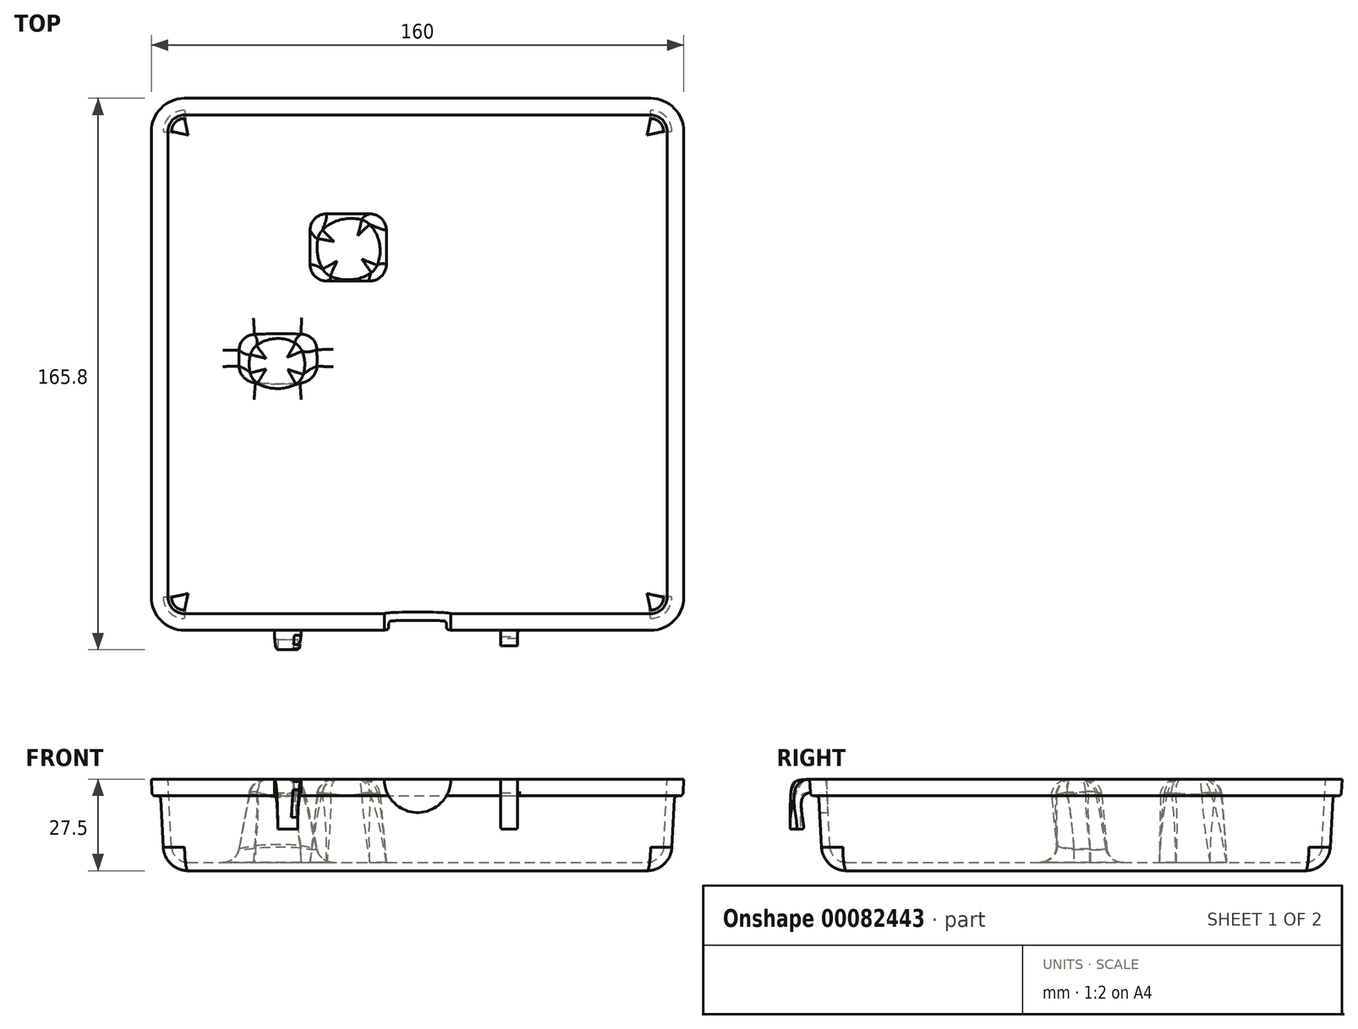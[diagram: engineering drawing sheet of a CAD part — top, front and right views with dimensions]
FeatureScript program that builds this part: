
annotation { "Feature Type Name" : "Feature", "Feature Type Description" : "" }
export const myFeature = defineFeature(function(context is Context, id is Id, definition is map)
    precondition{}
    {
        {
            var Q0;
            Q0=qCreatedBy(makeId("Top.planeOp"),FACE);
            var sketch = newSketch(context, id + "F0", { "sketchPlane" : qUnion([Q0])});
            skLineSegment(sketch, "E0.bottom", {"start": v(5, 0) * mm, "end": v(145, 0) * mm});
            skLineSegment(sketch, "E0.top", {"start": v(5, 150) * mm, "end": v(145, 150) * mm});
            skLineSegment(sketch, "E0.left", {"start": v(0, 5) * mm, "end": v(0, 145) * mm});
            skLineSegment(sketch, "E0.right", {"start": v(150, 5) * mm, "end": v(150, 145) * mm});
            skLineSegment(sketch, "E1.0", {"start": v(-5, 5) * mm, "end": v(-5, 145) * mm});
            skLineSegment(sketch, "E1.1", {"start": v(5, -5) * mm, "end": v(145, -5) * mm});
            skLineSegment(sketch, "E1.2", {"start": v(155, 5) * mm, "end": v(155, 145) * mm});
            skLineSegment(sketch, "E1.3", {"start": v(5, 155) * mm, "end": v(145, 155) * mm});
            skPoint(sketch, "E2.visualSharp", {"position": v(0, 150) * mm});
            skArc(sketch, "E2.filletArc", {"start": v(5, 150) * mm, "mid": v(1.46, 148.54) * mm, "end": v(0, 145) * mm});
            skPoint(sketch, "E3.visualSharp", {"position": v(150, 150) * mm});
            skArc(sketch, "E3.filletArc", {"start": v(150, 145) * mm, "mid": v(148.54, 148.54) * mm, "end": v(145, 150) * mm});
            skPoint(sketch, "E4.visualSharp", {"position": v(150, 0) * mm});
            skArc(sketch, "E4.filletArc", {"start": v(145, 0) * mm, "mid": v(148.54, 1.46) * mm, "end": v(150, 5) * mm});
            skPoint(sketch, "E5.visualSharp", {"position": v(0, 0) * mm});
            skArc(sketch, "E5.filletArc", {"start": v(0, 5) * mm, "mid": v(1.46, 1.46) * mm, "end": v(5, 0) * mm});
            skPoint(sketch, "E6.visualSharp", {"position": v(-5, 155) * mm});
            skArc(sketch, "E6.filletArc", {"start": v(5, 155) * mm, "mid": v(-2.07, 152.07) * mm, "end": v(-5, 145) * mm});
            skPoint(sketch, "E7.visualSharp", {"position": v(155, 155) * mm});
            skArc(sketch, "E7.filletArc", {"start": v(155, 145) * mm, "mid": v(152.07, 152.07) * mm, "end": v(145, 155) * mm});
            skPoint(sketch, "E8.visualSharp", {"position": v(155, -5) * mm});
            skArc(sketch, "E8.filletArc", {"start": v(145, -5) * mm, "mid": v(152.07, -2.07) * mm, "end": v(155, 5) * mm});
            skPoint(sketch, "E9.visualSharp", {"position": v(-5, -5) * mm});
            skArc(sketch, "E9.filletArc", {"start": v(-5, 5) * mm, "mid": v(-2.07, -2.07) * mm, "end": v(5, -5) * mm});
            skSolve(sketch);
        }
        {
            var Q0;
            Q0=makeQuery(id+"F0.imprint","IMPRINT",FACE,{"disambiguationData":[TD([[makeQuery(id+"F0.imprint","IMPRINT",EDGE,{"derivedFrom":sQuery(id+"F0.wireOp",EDGE,"E0.bottom")}),1.0]])]});
            extrude(context, id + "F1", {"entities" : qUnion([Q0]), "oppositeDirection" : true, "depth" : 25 * mm, "hasDraft" : true, "draftAngle" : 3 * degree, "draftPullDirection" : true});
        }
        {
            var Q0;
            Q0=makeQuery(id+"F1.opExtrude","SWEPT_EDGE",EDGE,{"disambiguationData":[OSD([sQuery(id+"F0.wireOp",EDGE,"E0.bottom"),sQuery(id+"F0.wireOp",EDGE,"E0.left")])]});
            var Q1;
            Q1=makeQuery(id+"F1.opExtrude","SWEPT_EDGE",EDGE,{"disambiguationData":[OSD([sQuery(id+"F0.wireOp",EDGE,"E0.bottom"),sQuery(id+"F0.wireOp",EDGE,"E0.right")])]});
            var Q2;
            Q2=makeQuery(id+"F1.opExtrude","SWEPT_EDGE",EDGE,{"disambiguationData":[OSD([sQuery(id+"F0.wireOp",EDGE,"E0.top"),sQuery(id+"F0.wireOp",EDGE,"E0.left")])]});
            var Q3;
            Q3=makeQuery(id+"F1.opExtrude","SWEPT_EDGE",EDGE,{"disambiguationData":[OSD([sQuery(id+"F0.wireOp",EDGE,"E0.top"),sQuery(id+"F0.wireOp",EDGE,"E0.right")])]});
            var Q4;
            Q4=makeQuery(id+"F1.opExtrude","CAP_FACE",FACE,{"disambiguationData":[OSD([sQuery(id+"F0.wireOp",EDGE,"E0.bottom"),sQuery(id+"F0.wireOp",EDGE,"E0.top"),sQuery(id+"F0.wireOp",EDGE,"E0.left"),sQuery(id+"F0.wireOp",EDGE,"E0.right")])],"isStart":false});
            fillet(context, id + "F2", {"entities" : qUnion([Q0, Q1, Q2, Q3, Q4]), "radius" : 5 * mm, "tangentPropagation" : true, "allowEdgeOverflow" : false});
        }
        {
            var Q0;
            Q0=makeQuery(id+"F1.opExtrude","CAP_FACE",FACE,{"disambiguationData":[OSD([sQuery(id+"F0.wireOp",EDGE,"E0.bottom"),sQuery(id+"F0.wireOp",EDGE,"E0.top"),sQuery(id+"F0.wireOp",EDGE,"E0.left"),sQuery(id+"F0.wireOp",EDGE,"E0.right")])],"isStart":true});
            shell(context, id + "F3", {"entities" : qUnion([Q0]), "thickness" : 2.5 * mm, "oppositeDirection" : true});
        }
        {
            var Q0;
            Q0=makeQuery(id+"F0.imprint","IMPRINT",FACE,{"disambiguationData":[TD([[makeQuery(id+"F0.imprint","IMPRINT",EDGE,{"derivedFrom":sQuery(id+"F0.wireOp",EDGE,"E0.bottom")}),-1.0]])]});
            extrude(context, id + "F4", {"entities" : qUnion([Q0]), "operationType" : NewBodyOperationType.ADD, "oppositeDirection" : true, "depth" : 5 * mm, "hasDraft" : true, "draftAngle" : 3 * degree, "draftPullDirection" : true});
        }
        {
            var Q0;
            {var subQ0=sQuery(id+"F0.wireOp",EDGE,"E0.bottom");Q0=makeQuery(id+"F4.boolean.opBoolean","INTERSECT",EDGE,{"derivedFrom":[makeQuery(id+"F1.opExtrude","SWEPT_FACE",FACE,{"disambiguationData":[OSD([subQ0])]}),makeQuery(id+"F4.opExtrude","CAP_FACE",FACE,{"disambiguationData":[OSD([subQ0,sQuery(id+"F0.wireOp",EDGE,"E0.top"),sQuery(id+"F0.wireOp",EDGE,"E0.left"),sQuery(id+"F0.wireOp",EDGE,"E0.right"),sQuery(id+"F0.wireOp",EDGE,"E1.0"),sQuery(id+"F0.wireOp",EDGE,"E1.1"),sQuery(id+"F0.wireOp",EDGE,"E1.2"),sQuery(id+"F0.wireOp",EDGE,"E1.3"),sQuery(id+"F0.wireOp",EDGE,"E2.filletArc"),sQuery(id+"F0.wireOp",EDGE,"E3.filletArc"),sQuery(id+"F0.wireOp",EDGE,"E4.filletArc"),sQuery(id+"F0.wireOp",EDGE,"E5.filletArc"),sQuery(id+"F0.wireOp",EDGE,"E6.filletArc"),sQuery(id+"F0.wireOp",EDGE,"E7.filletArc"),sQuery(id+"F0.wireOp",EDGE,"E8.filletArc"),sQuery(id+"F0.wireOp",EDGE,"E9.filletArc")])],"isStart":false})]});}
            var Q1;
            Q1=makeQuery(id+"F4.opExtrude","CAP_EDGE",EDGE,{"disambiguationData":[OSD([sQuery(id+"F0.wireOp",EDGE,"E1.1")])],"isStart":false});
            fillet(context, id + "F5", {"entities" : qUnion([Q0, Q1]), "radius" : 1 * mm, "tangentPropagation" : true, "allowEdgeOverflow" : false});
        }
        {
            var Q0;
            Q0=qCreatedBy(makeId("Front.planeOp"),FACE);
            var sketch = newSketch(context, id + "F6", { "sketchPlane" : qUnion([Q0])});
            skCircle(sketch, "E10", {"center": v(75, 0) * mm, "radius": 10 * mm});
            skSolve(sketch);
        }
        {
            var Q0;
            Q0 = qSketchRegion(id + "F6", true);
            extrude(context, id + "F7", {"entities" : qUnion([Q0]), "operationType" : NewBodyOperationType.REMOVE, "endBound" : BoundingType.SYMMETRIC, "depth" : 25 * mm});
        }
        {
            var Q0;
            Q0=qCreatedBy(makeId("Top.planeOp"),FACE);
            cPlane(context, id + "F8", {"entities" : qUnion([Q0]), "cplaneType" : CPlaneType.OFFSET, "offset" : 15 * mm, "oppositeDirection" : true, "width" : 150 * mm, "height" : 150 * mm});
        }
        {
            var Q0;
            {var subQ0=sQuery(id+"F0.wireOp",EDGE,"E1.1");var subQ1=sQuery(id+"F0.wireOp",EDGE,"E8.filletArc");Q0=makeQuery(id+"F7.boolean.opBoolean","SPLIT",FACE,{"disambiguationData":[TD([makeQuery(id+"F4.opExtrude","SWEPT_FACE",FACE,{"disambiguationData":[OSD([subQ1])]})])],"derivedFrom":makeQuery(id+"F4.opExtrude","SWEPT_FACE",FACE,{"disambiguationData":[OSD([subQ0])]})});}
            var sketch = newSketch(context, id + "F9", { "sketchPlane" : qUnion([Q0])});
            skLineSegment(sketch, "E11.bottom", {"start": v(100, 0.26) * mm, "end": v(105, 0.26) * mm});
            skLineSegment(sketch, "E11.top", {"start": v(100, -3.8) * mm, "end": v(105, -3.8) * mm});
            skLineSegment(sketch, "E11.left", {"start": v(100, 0.26) * mm, "end": v(100, -3.8) * mm});
            skLineSegment(sketch, "E11.right", {"start": v(105, 0.26) * mm, "end": v(105, -3.8) * mm});
            skSolve(sketch);
        }
        {
            var Q0;
            Q0=qCreatedBy(id+"F8.planeOp",FACE);
            var sketch = newSketch(context, id + "F10", { "sketchPlane" : qUnion([Q0])});
            skLineSegment(sketch, "E12.bottom", {"start": v(100, -6.79) * mm, "end": v(105, -6.79) * mm});
            skLineSegment(sketch, "E12.top", {"start": v(100, -8.79) * mm, "end": v(105, -8.79) * mm});
            skLineSegment(sketch, "E12.left", {"start": v(100, -6.79) * mm, "end": v(100, -8.79) * mm});
            skLineSegment(sketch, "E12.right", {"start": v(105, -6.79) * mm, "end": v(105, -8.79) * mm});
            skSolve(sketch);
        }
        {
            var Q1;
            Q1=makeQuery(id+"F9.imprint","IMPRINT",FACE,{"disambiguationData":[TD([[makeQuery(id+"F9.imprint","IMPRINT",EDGE,{"derivedFrom":sQuery(id+"F9.wireOp",EDGE,"E11.bottom")}),-1.0]])]});
            var Q2;
            Q2=makeQuery(id+"F10.imprint","IMPRINT",FACE,{"disambiguationData":[TD([[makeQuery(id+"F10.imprint","IMPRINT",EDGE,{"derivedFrom":sQuery(id+"F10.wireOp",EDGE,"E12.bottom")}),-1.0]])]});
            loft(context, id + "F11", {"operationType" : NewBodyOperationType.ADD, "startCondition" : LoftEndDerivativeType.NORMAL_TO_PROFILE, "startMagnitude" : 4, "endCondition" : LoftEndDerivativeType.NORMAL_TO_PROFILE, "endMagnitude" : 1, "sheetProfilesArray" : [{ "sheetProfileEntities" : qUnion([Q1]) }, { "sheetProfileEntities" : qUnion([Q2]) }]});
        }
        {
            var Q0;
            Q0=makeQuery(id+"F11.opLoft","MID_CAP_EDGE",EDGE,{"disambiguationData":[OSD([sQuery(id+"F0.wireOp",EDGE,"E1.1"),sQuery(id+"F9.wireOp",EDGE,"E11.bottom"),sQuery(id+"F9.wireOp",EDGE,"E11.top"),sQuery(id+"F9.wireOp",EDGE,"E11.right")])],"capPos":0.0});
            fillet(context, id + "F12", {"entities" : qUnion([Q0]), "radius" : 1 * mm, "tangentPropagation" : true, "allowEdgeOverflow" : false});
        }
        {
            var Q0;
            Q0=makeQuery(id+"F11.opLoft","CAP_FACE",FACE,{"disambiguationData":[OSD([makeQuery(id+"F10.imprint","IMPRINT",FACE,{"disambiguationData":[TD([[makeQuery(id+"F10.imprint","IMPRINT",EDGE,{"derivedFrom":sQuery(id+"F10.wireOp",EDGE,"E12.bottom")}),-1.0]])]})])],"isStart":true});
            fillet(context, id + "F13", {"entities" : qUnion([Q0]), "radius" : .5 * mm, "tangentPropagation" : true, "allowEdgeOverflow" : false});
        }
        {
            var Q0;
            Q0=makeQuery(id+"F3.opShell","OFFSET_FACE",FACE,{"disambiguationData":[OSD([sQuery(id+"F0.wireOp",EDGE,"E0.bottom"),sQuery(id+"F0.wireOp",EDGE,"E0.top"),sQuery(id+"F0.wireOp",EDGE,"E0.left"),sQuery(id+"F0.wireOp",EDGE,"E0.right"),sQuery(id+"F0.wireOp",EDGE,"E2.filletArc"),sQuery(id+"F0.wireOp",EDGE,"E3.filletArc"),sQuery(id+"F0.wireOp",EDGE,"E4.filletArc"),sQuery(id+"F0.wireOp",EDGE,"E5.filletArc")])]});
            var sketch = newSketch(context, id + "F14", { "sketchPlane" : qUnion([Q0])});
            skLineSegment(sketch, "E13.bottom", {"start": v(42.7, 100.07) * mm, "end": v(65.63, 100.07) * mm});
            skLineSegment(sketch, "E13.top", {"start": v(42.7, 120.25) * mm, "end": v(65.63, 120.25) * mm});
            skLineSegment(sketch, "E13.left", {"start": v(42.7, 100.07) * mm, "end": v(42.7, 120.25) * mm});
            skLineSegment(sketch, "E13.right", {"start": v(65.63, 100.07) * mm, "end": v(65.63, 120.25) * mm});
            skSolve(sketch);
        }
        {
            var Q0;
            Q0=qCreatedBy(makeId("Top.planeOp"),FACE);
            var sketch = newSketch(context, id + "F15", { "sketchPlane" : qUnion([Q0])});
            skArc(sketch, "E14", {"start": v(48.26, 102.79) * mm, "mid": v(55.2, 100.54) * mm, "end": v(61.55, 104.16) * mm});
            skArc(sketch, "E15", {"start": v(58.35, 117.61) * mm, "mid": v(51.16, 118.02) * mm, "end": v(45.95, 113.06) * mm});
            skArc(sketch, "E16", {"start": v(45.95, 113.06) * mm, "mid": v(45.46, 107.55) * mm, "end": v(48.26, 102.79) * mm});
            skArc(sketch, "E17", {"start": v(61.55, 104.16) * mm, "mid": v(63.08, 111.63) * mm, "end": v(58.35, 117.61) * mm});
            skSolve(sketch);
        }
        {
            var Q1;
            Q1=makeQuery(id+"F14.imprint","IMPRINT",FACE,{"disambiguationData":[TD([[makeQuery(id+"F14.imprint","IMPRINT",EDGE,{"derivedFrom":sQuery(id+"F14.wireOp",EDGE,"E13.bottom")}),1.0]])]});
            var Q2;
            Q2=makeQuery(id+"F15.imprint","IMPRINT",FACE,{"disambiguationData":[TD([[makeQuery(id+"F15.imprint","IMPRINT",EDGE,{"derivedFrom":sQuery(id+"F15.wireOp",EDGE,"E14")}),1.0]])]});
            var Q3;
            Q3=sQuery(id+"F14.wireOp",VERTEX,"E13.right.start");
            var Q4;
            Q4=sQuery(id+"F15.wireOp",VERTEX,"E16.end");
            loft(context, id + "F16", {"operationType" : NewBodyOperationType.ADD, "sheetProfilesArray" : [{ "sheetProfileEntities" : qUnion([Q1]) }, { "sheetProfileEntities" : qUnion([Q2]) }], "connections" : [{ "connectionEntities" : qUnion([Q3, Q4]), "connectionEdgeQueries" : qUnion([]), "connectionEdgeParameters" : [] }]});
        }
        {
            var Q0;
            Q0=makeQuery(id+"F16.opLoft","SWEPT_EDGE",EDGE,{"disambiguationData":[OSD([sQuery(id+"F14.wireOp",EDGE,"E13.bottom"),sQuery(id+"F14.wireOp",EDGE,"E13.left"),sQuery(id+"F15.wireOp",EDGE,"E14"),sQuery(id+"F15.wireOp",EDGE,"E16")])]});
            var Q1;
            Q1=makeQuery(id+"F16.opLoft","SWEPT_EDGE",EDGE,{"disambiguationData":[OSD([sQuery(id+"F14.wireOp",EDGE,"E13.bottom"),sQuery(id+"F14.wireOp",EDGE,"E13.right"),sQuery(id+"F15.wireOp",EDGE,"E14"),sQuery(id+"F15.wireOp",EDGE,"E17")])]});
            var Q2;
            Q2=makeQuery(id+"F16.opLoft","SWEPT_EDGE",EDGE,{"disambiguationData":[OSD([sQuery(id+"F14.wireOp",EDGE,"E13.top"),sQuery(id+"F14.wireOp",EDGE,"E13.right"),sQuery(id+"F15.wireOp",EDGE,"E15"),sQuery(id+"F15.wireOp",EDGE,"E17")])]});
            var Q3;
            Q3=makeQuery(id+"F16.opLoft","SWEPT_EDGE",EDGE,{"disambiguationData":[OSD([sQuery(id+"F14.wireOp",EDGE,"E13.top"),sQuery(id+"F14.wireOp",EDGE,"E13.left"),sQuery(id+"F15.wireOp",EDGE,"E15"),sQuery(id+"F15.wireOp",EDGE,"E16")])]});
            fillet(context, id + "F17", {"entities" : qUnion([Q0, Q1, Q2, Q3]), "radius" : 5 * mm, "tangentPropagation" : true, "allowEdgeOverflow" : false});
        }
        {
            var Q0;
            Q0=makeQuery(id+"F16.opLoft","MID_CAP_EDGE",EDGE,{"disambiguationData":[OSD([sQuery(id+"F14.wireOp",EDGE,"E13.bottom"),sQuery(id+"F14.wireOp",EDGE,"E13.top"),sQuery(id+"F14.wireOp",EDGE,"E13.left")])],"capPos":0.0});
            var Q1;
            Q1=makeQuery(id+"F16.opLoft","MID_CAP_EDGE",EDGE,{"disambiguationData":[OSD([sQuery(id+"F15.wireOp",EDGE,"E14"),sQuery(id+"F15.wireOp",EDGE,"E15"),sQuery(id+"F15.wireOp",EDGE,"E16")])],"capPos":1.0});
            fillet(context, id + "F18", {"entities" : qUnion([Q0, Q1]), "radius" : 5 * mm, "tangentPropagation" : true, "allowEdgeOverflow" : false});
        }
        {
            var Q0;
            Q0=makeQuery(id+"F14.imprint","IMPRINT",FACE,{"disambiguationData":[TD([[makeQuery(id+"F14.imprint","IMPRINT",EDGE,{"derivedFrom":sQuery(id+"F14.wireOp",EDGE,"E13.bottom")}),-1.0]])]});
            var sketch = newSketch(context, id + "F19", { "sketchPlane" : qUnion([Q0])});
            skLineSegment(sketch, "E18.bottom", {"start": v(20.62, 69.63) * mm, "end": v(45.62, 69.63) * mm});
            skLineSegment(sketch, "E18.top", {"start": v(20.62, 84.63) * mm, "end": v(45.62, 84.63) * mm});
            skLineSegment(sketch, "E18.left", {"start": v(20.62, 69.63) * mm, "end": v(20.62, 84.63) * mm});
            skLineSegment(sketch, "E18.right", {"start": v(45.62, 69.63) * mm, "end": v(45.62, 84.63) * mm});
            skSolve(sketch);
        }
        {
            var Q0;
            Q0=qCreatedBy(makeId("Top.planeOp"),FACE);
            var sketch = newSketch(context, id + "F20", { "sketchPlane" : qUnion([Q0])});
            skArc(sketch, "E19", {"start": v(38.94, 70.46) * mm, "mid": v(40.28, 75.1) * mm, "end": v(38.54, 79.62) * mm});
            skArc(sketch, "E20", {"start": v(38.54, 79.62) * mm, "mid": v(32.07, 82.32) * mm, "end": v(26.16, 78.56) * mm});
            skArc(sketch, "E21", {"start": v(26.16, 78.56) * mm, "mid": v(25.14, 74.72) * mm, "end": v(26.21, 70.9) * mm});
            skArc(sketch, "E22", {"start": v(26.21, 70.9) * mm, "mid": v(32.46, 67.2) * mm, "end": v(38.94, 70.46) * mm});
            skLineSegment(sketch, "E23", {"start": v(26.16, 78.56) * mm, "end": v(32.72, 74.78) * mm, "construction": true});
            skLineSegment(sketch, "E24", {"start": v(38.54, 79.62) * mm, "end": v(32.72, 74.78) * mm, "construction": true});
            skLineSegment(sketch, "E25", {"start": v(38.94, 70.46) * mm, "end": v(32.72, 74.78) * mm, "construction": true});
            skLineSegment(sketch, "E26", {"start": v(32.72, 74.78) * mm, "end": v(26.21, 70.9) * mm, "construction": true});
            skLineSegment(sketch, "E27", {"start": v(32.72, 74.78) * mm, "end": v(18.64, 74.78) * mm, "construction": true});
            skSolve(sketch);
        }
        {
            var Q1;
            Q1=makeQuery(id+"F19.imprint","IMPRINT",FACE,{"disambiguationData":[TD([[makeQuery(id+"F19.imprint","IMPRINT",EDGE,{"derivedFrom":sQuery(id+"F19.wireOp",EDGE,"E18.bottom")}),1.0]])]});
            var Q2;
            Q2=makeQuery(id+"F20.imprint","IMPRINT",FACE,{"disambiguationData":[TD([[makeQuery(id+"F20.imprint","IMPRINT",EDGE,{"derivedFrom":sQuery(id+"F20.wireOp",EDGE,"E19")}),1.0]])]});
            loft(context, id + "F21", {"operationType" : NewBodyOperationType.ADD, "sheetProfilesArray" : [{ "sheetProfileEntities" : qUnion([Q1]) }, { "sheetProfileEntities" : qUnion([Q2]) }]});
        }
        {
            var Q0;
            Q0=makeQuery(id+"F21.opLoft","SWEPT_EDGE",EDGE,{"disambiguationData":[OSD([sQuery(id+"F19.wireOp",EDGE,"E18.bottom"),sQuery(id+"F19.wireOp",EDGE,"E18.left"),sQuery(id+"F20.wireOp",EDGE,"E21"),sQuery(id+"F20.wireOp",EDGE,"E22")])]});
            var Q1;
            Q1=makeQuery(id+"F21.opLoft","SWEPT_EDGE",EDGE,{"disambiguationData":[OSD([sQuery(id+"F19.wireOp",EDGE,"E18.bottom"),sQuery(id+"F19.wireOp",EDGE,"E18.right"),sQuery(id+"F20.wireOp",EDGE,"E19"),sQuery(id+"F20.wireOp",EDGE,"E22")])]});
            var Q2;
            Q2=makeQuery(id+"F21.opLoft","SWEPT_EDGE",EDGE,{"disambiguationData":[OSD([sQuery(id+"F19.wireOp",EDGE,"E18.top"),sQuery(id+"F19.wireOp",EDGE,"E18.right"),sQuery(id+"F20.wireOp",EDGE,"E19"),sQuery(id+"F20.wireOp",EDGE,"E20")])]});
            var Q3;
            Q3=makeQuery(id+"F21.opLoft","SWEPT_EDGE",EDGE,{"disambiguationData":[OSD([sQuery(id+"F19.wireOp",EDGE,"E18.top"),sQuery(id+"F19.wireOp",EDGE,"E18.left"),sQuery(id+"F20.wireOp",EDGE,"E20"),sQuery(id+"F20.wireOp",EDGE,"E21")])]});
            fillet(context, id + "F22", {"entities" : qUnion([Q0, Q1, Q2, Q3]), "radius" : 5 * mm, "tangentPropagation" : true, "allowEdgeOverflow" : false});
        }
        {
            var Q0;
            Q0=makeQuery(id+"F22.opFillet","BLEND_EDGE",EDGE,{"blendedFrom":[makeQuery(id+"F21.opLoft","SWEPT_EDGE",EDGE,{"disambiguationData":[OSD([sQuery(id+"F19.wireOp",EDGE,"E18.bottom"),sQuery(id+"F19.wireOp",EDGE,"E18.right"),sQuery(id+"F20.wireOp",EDGE,"E19"),sQuery(id+"F20.wireOp",EDGE,"E22")])]}),makeQuery(id+"F3.opShell","OFFSET_FACE",FACE,{"disambiguationData":[OSD([sQuery(id+"F0.wireOp",EDGE,"E0.bottom"),sQuery(id+"F0.wireOp",EDGE,"E0.top"),sQuery(id+"F0.wireOp",EDGE,"E0.left"),sQuery(id+"F0.wireOp",EDGE,"E0.right"),sQuery(id+"F0.wireOp",EDGE,"E2.filletArc"),sQuery(id+"F0.wireOp",EDGE,"E3.filletArc"),sQuery(id+"F0.wireOp",EDGE,"E4.filletArc"),sQuery(id+"F0.wireOp",EDGE,"E5.filletArc")])]})],"blendedInto":[makeQuery(id+"F3.opShell","OFFSET_FACE",FACE,{"disambiguationData":[OSD([sQuery(id+"F0.wireOp",EDGE,"E0.bottom"),sQuery(id+"F0.wireOp",EDGE,"E0.top"),sQuery(id+"F0.wireOp",EDGE,"E0.left"),sQuery(id+"F0.wireOp",EDGE,"E0.right"),sQuery(id+"F0.wireOp",EDGE,"E2.filletArc"),sQuery(id+"F0.wireOp",EDGE,"E3.filletArc"),sQuery(id+"F0.wireOp",EDGE,"E4.filletArc"),sQuery(id+"F0.wireOp",EDGE,"E5.filletArc")])]})]});
            var Q1;
            Q1=makeQuery(id+"F21.opLoft","MID_CAP_EDGE",EDGE,{"disambiguationData":[OSD([sQuery(id+"F20.wireOp",EDGE,"E19"),sQuery(id+"F20.wireOp",EDGE,"E21"),sQuery(id+"F20.wireOp",EDGE,"E22")])],"capPos":1.0});
            fillet(context, id + "F23", {"entities" : qUnion([Q0, Q1]), "radius" : 5 * mm, "tangentPropagation" : true, "allowEdgeOverflow" : false});
        }
        {
            var Q0;
            {var subQ0=sQuery(id+"F0.wireOp",EDGE,"E1.1");var subQ1=sQuery(id+"F0.wireOp",EDGE,"E9.filletArc");Q0=makeQuery(id+"F7.boolean.opBoolean","SPLIT",FACE,{"disambiguationData":[TD([makeQuery(id+"F4.opExtrude","SWEPT_FACE",FACE,{"disambiguationData":[OSD([subQ1])]})])],"derivedFrom":makeQuery(id+"F4.opExtrude","SWEPT_FACE",FACE,{"disambiguationData":[OSD([subQ0])]})});}
            var sketch = newSketch(context, id + "F24", { "sketchPlane" : qUnion([Q0])});
            skLineSegment(sketch, "E28.bottom", {"start": v(32, -3.8) * mm, "end": v(40, -3.8) * mm});
            skLineSegment(sketch, "E28.top", {"start": v(32, 0.26) * mm, "end": v(40, 0.26) * mm});
            skLineSegment(sketch, "E28.left", {"start": v(32, -3.8) * mm, "end": v(32, 0.26) * mm});
            skLineSegment(sketch, "E28.right", {"start": v(40, -3.8) * mm, "end": v(40, 0.26) * mm});
            skLineSegment(sketch, "E29.bottom", {"start": v(38, 0.76) * mm, "end": v(42, 0.76) * mm});
            skLineSegment(sketch, "E29.top", {"start": v(38, 2.76) * mm, "end": v(42, 2.76) * mm});
            skLineSegment(sketch, "E29.left", {"start": v(38, 0.76) * mm, "end": v(38, 2.76) * mm});
            skLineSegment(sketch, "E29.right", {"start": v(42, 0.76) * mm, "end": v(42, 2.76) * mm});
            skSolve(sketch);
        }
        {
            var Q0;
            Q0=qCreatedBy(id+"F8.planeOp",FACE);
            var sketch = newSketch(context, id + "F25", { "sketchPlane" : qUnion([Q0])});
            skLineSegment(sketch, "E30.bottom", {"start": v(33, -7.79) * mm, "end": v(39, -7.79) * mm});
            skLineSegment(sketch, "E30.top", {"start": v(33, -10.79) * mm, "end": v(39, -10.79) * mm});
            skLineSegment(sketch, "E30.left", {"start": v(33, -7.79) * mm, "end": v(33, -10.79) * mm});
            skLineSegment(sketch, "E30.right", {"start": v(39, -7.79) * mm, "end": v(39, -10.79) * mm});
            skLineSegment(sketch, "E31.bottom", {"start": v(37, -11.04) * mm, "end": v(42.04, -11.04) * mm});
            skLineSegment(sketch, "E31.top", {"start": v(37, -13.04) * mm, "end": v(42.04, -13.04) * mm});
            skLineSegment(sketch, "E31.left", {"start": v(37, -11.04) * mm, "end": v(37, -13.04) * mm});
            skLineSegment(sketch, "E31.right", {"start": v(42.04, -11.04) * mm, "end": v(42.04, -13.04) * mm});
            skSolve(sketch);
        }
        {
            var Q1;
            {var subQ0=sQuery(id+"F24.wireOp",EDGE,"E28.left");Q1=makeQuery(id+"F24.imprint","IMPRINT",FACE,{"disambiguationData":[TD([[makeQuery(id+"F24.imprint","IMPRINT",EDGE,{"derivedFrom":subQ0}),-1.0]])]});}
            var Q2;
            Q2=makeQuery(id+"F25.imprint","IMPRINT",FACE,{"disambiguationData":[TD([[makeQuery(id+"F25.imprint","IMPRINT",EDGE,{"derivedFrom":sQuery(id+"F25.wireOp",EDGE,"E30.bottom")}),-1.0]])]});
            loft(context, id + "F26", {"operationType" : NewBodyOperationType.ADD, "startCondition" : LoftEndDerivativeType.NORMAL_TO_PROFILE, "startMagnitude" : 2.5, "endCondition" : LoftEndDerivativeType.NORMAL_TO_PROFILE, "endMagnitude" : 3, "sheetProfilesArray" : [{ "sheetProfileEntities" : qUnion([Q1]) }, { "sheetProfileEntities" : qUnion([Q2]) }]});
        }
        {
            var Q1;
            Q1=makeQuery(id+"F24.imprint","IMPRINT",FACE,{"disambiguationData":[TD([[makeQuery(id+"F24.imprint","IMPRINT",EDGE,{"derivedFrom":sQuery(id+"F24.wireOp",EDGE,"E29.bottom")}),1.0]])]});
            var Q2;
            Q2=makeQuery(id+"F25.imprint","IMPRINT",FACE,{"disambiguationData":[TD([[makeQuery(id+"F25.imprint","IMPRINT",EDGE,{"derivedFrom":sQuery(id+"F25.wireOp",EDGE,"E31.bottom")}),-1.0]])]});
            loft(context, id + "F27", {"operationType" : NewBodyOperationType.REMOVE, "startCondition" : LoftEndDerivativeType.NORMAL_TO_PROFILE, "startMagnitude" : 1.5, "endCondition" : LoftEndDerivativeType.NORMAL_TO_PROFILE, "endMagnitude" : 1, "sheetProfilesArray" : [{ "sheetProfileEntities" : qUnion([Q1]) }, { "sheetProfileEntities" : qUnion([Q2]) }]});
        }
    });
